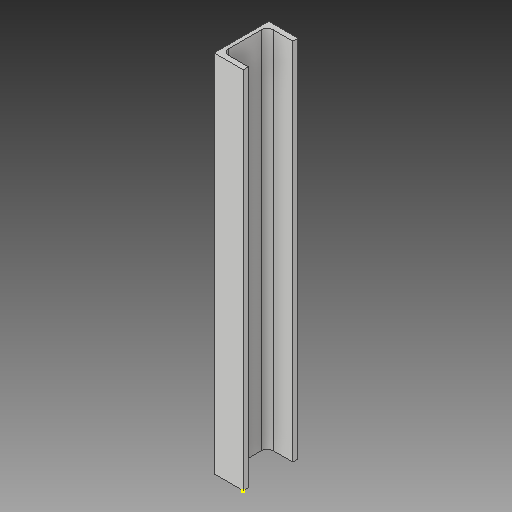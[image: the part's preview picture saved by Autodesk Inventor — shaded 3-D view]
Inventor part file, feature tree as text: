
AUTODESK INVENTOR PART (.ipt)
format: ipt  version: 2019 (Build 230136000, 136)  size: 97,280 bytes
history: native  units: in
note: dims shown in document units (in); Inventor stores cm internally (conversion verified against a paired STEP export)
features: other x3, sketch x2
ambient origin geometry x8: Origin, YZ Plane, XZ Plane, XY Plane, X Axis, Y Axis, Z Axis, Center Point
bodies: Solid1 (feature_tree)
feature tree (5):
  other  "Channel2_MIR.ipt"
  other  "Solid1::Channel2_MIR.ipt"
  other  "TaggingFeature1"
  sketch  "Sketch1"  dims[d0=0.3937in]
  sketch  "Sketch2"
